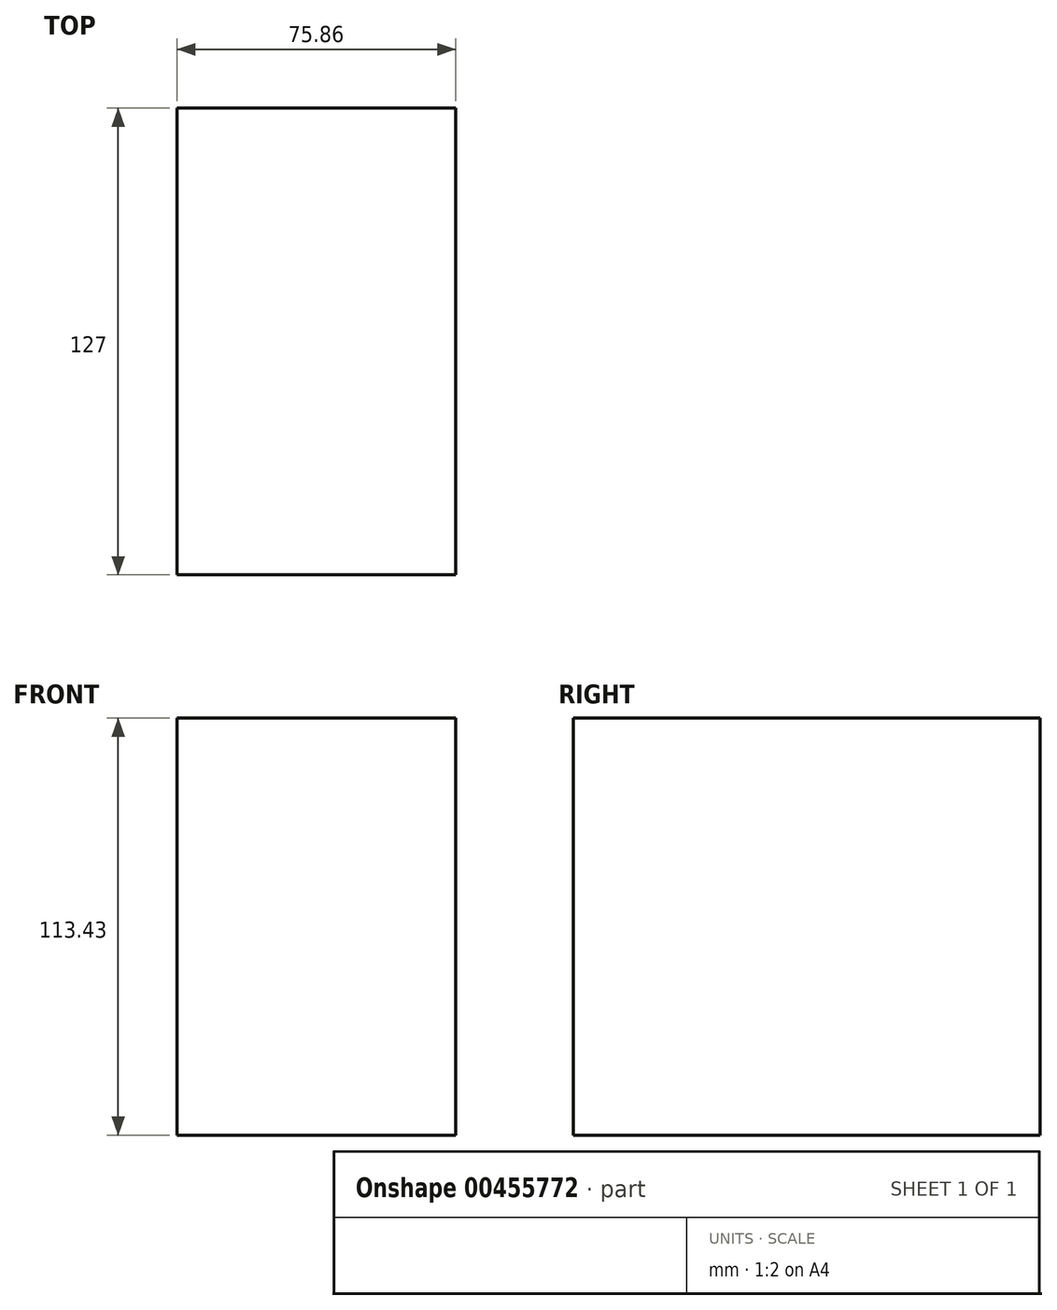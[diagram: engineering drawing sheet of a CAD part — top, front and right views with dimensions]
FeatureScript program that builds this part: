
annotation { "Feature Type Name" : "Feature", "Feature Type Description" : "" }
export const myFeature = defineFeature(function(context is Context, id is Id, definition is map)
    precondition{}
    {
        {
            var Q0;
            Q0=qCreatedBy(makeId("Front.planeOp"),FACE);
            var sketch = newSketch(context, id + "F0", { "sketchPlane" : qUnion([Q0])});
            skLineSegment(sketch, "E0.bottom", {"start": v(28.78, 55.86) * mm, "end": v(-47.08, 55.86) * mm});
            skLineSegment(sketch, "E0.top", {"start": v(28.78, -57.57) * mm, "end": v(-47.08, -57.57) * mm});
            skLineSegment(sketch, "E0.left", {"start": v(28.78, 55.86) * mm, "end": v(28.78, -57.57) * mm});
            skLineSegment(sketch, "E0.right", {"start": v(-47.08, 55.86) * mm, "end": v(-47.08, -57.57) * mm});
            skSolve(sketch);
        }
        {
            var Q0;
            Q0 = qSketchRegion(id + "F0", true);
            extrude(context, id + "F1", {"entities" : qUnion([Q0]), "depth" : 127 * mm});
        }
    });
